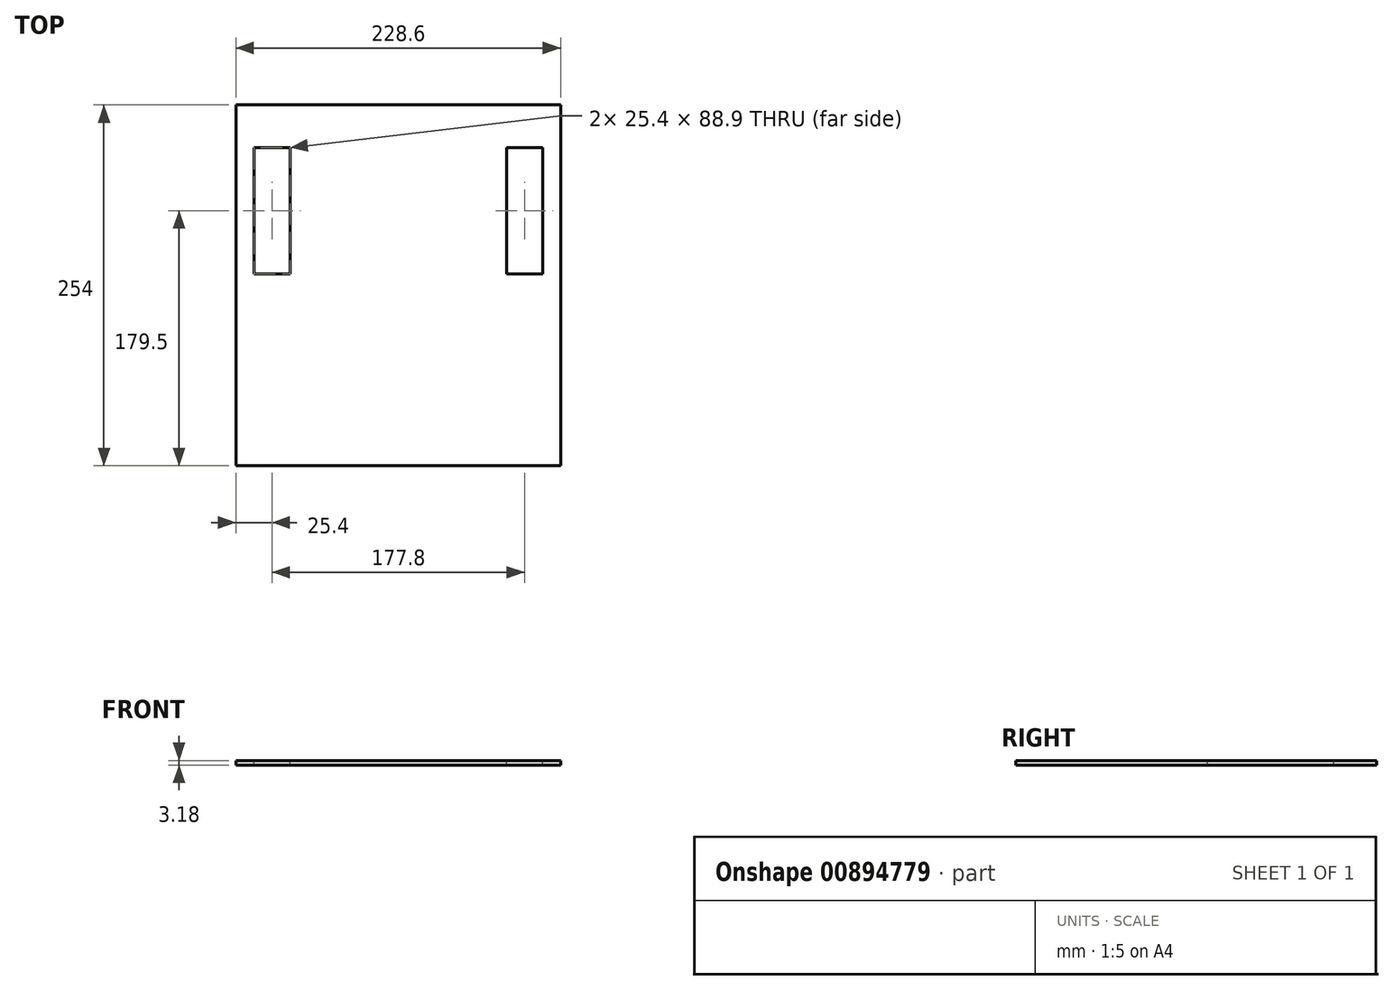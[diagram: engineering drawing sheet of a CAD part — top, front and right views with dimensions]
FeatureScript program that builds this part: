
annotation { "Feature Type Name" : "Feature", "Feature Type Description" : "" }
export const myFeature = defineFeature(function(context is Context, id is Id, definition is map)
    precondition{}
    {
        {
            var Q0;
            Q0=qCreatedBy(makeId("Top.planeOp"),FACE);
            var sketch = newSketch(context, id + "F0", { "sketchPlane" : qUnion([Q0])});
            skLineSegment(sketch, "E0.bottom", {"start": v(114.3, -127) * mm, "end": v(-114.3, -127) * mm});
            skLineSegment(sketch, "E0.top", {"start": v(114.3, 127) * mm, "end": v(-114.3, 127) * mm});
            skLineSegment(sketch, "E0.left", {"start": v(114.3, -127) * mm, "end": v(114.3, 127) * mm});
            skLineSegment(sketch, "E0.right", {"start": v(-114.3, -127) * mm, "end": v(-114.3, 127) * mm});
            skPoint(sketch, "E0.middle", {"position": v(0, 0) * mm});
            skSolve(sketch);
        }
        {
            var Q0;
            Q0=makeQuery(id+"F0.imprint","IMPRINT",FACE,{"disambiguationData":[TD([[makeQuery(id+"F0.imprint","IMPRINT",EDGE,{"derivedFrom":sQuery(id+"F0.wireOp",EDGE,"E0.bottom")}),-1.0]])]});
            extrude(context, id + "F1", {"entities" : qUnion([Q0]), "depth" : 3.17 * mm, "offsetDistance" : 25.4 * mm});
        }
        {
            var Q0;
            Q0=makeQuery(id+"F1.opExtrude","CAP_FACE",FACE,{"disambiguationData":[OSD([sQuery(id+"F0.wireOp",EDGE,"E0.bottom"),sQuery(id+"F0.wireOp",EDGE,"E0.top"),sQuery(id+"F0.wireOp",EDGE,"E0.left"),sQuery(id+"F0.wireOp",EDGE,"E0.right")])],"isStart":false});
            var sketch = newSketch(context, id + "F2", { "sketchPlane" : qUnion([Q0])});
            skLineSegment(sketch, "E1.bottom", {"start": v(-101.6, 96.95) * mm, "end": v(-76.2, 96.95) * mm});
            skLineSegment(sketch, "E1.top", {"start": v(-101.6, 8.05) * mm, "end": v(-76.2, 8.05) * mm});
            skLineSegment(sketch, "E1.left", {"start": v(-101.6, 96.95) * mm, "end": v(-101.6, 8.05) * mm});
            skLineSegment(sketch, "E1.right", {"start": v(-76.2, 96.95) * mm, "end": v(-76.2, 8.05) * mm});
            skLineSegment(sketch, "E2.MirrorCS", {"start": v(76.2, 96.95) * mm, "end": v(76.2, 8.05) * mm});
            skLineSegment(sketch, "E3.MirrorCS", {"start": v(101.6, 8.05) * mm, "end": v(76.2, 8.05) * mm});
            skLineSegment(sketch, "E4.MirrorCS", {"start": v(101.6, 96.95) * mm, "end": v(101.6, 8.05) * mm});
            skLineSegment(sketch, "E5.MirrorCS", {"start": v(101.6, 96.95) * mm, "end": v(76.2, 96.95) * mm});
            skSolve(sketch);
        }
        {
            var Q0;
            Q0=makeQuery(id+"F2.imprint","IMPRINT",FACE,{"disambiguationData":[TD([[makeQuery(id+"F2.imprint","IMPRINT",EDGE,{"derivedFrom":sQuery(id+"F2.wireOp",EDGE,"E1.bottom")}),-1.0]])]});
            var Q1;
            Q1=makeQuery(id+"F2.imprint","IMPRINT",FACE,{"disambiguationData":[TD([[makeQuery(id+"F2.imprint","IMPRINT",EDGE,{"derivedFrom":sQuery(id+"F2.wireOp",EDGE,"E2.MirrorCS")}),1.0]])]});
            extrude(context, id + "F3", {"entities" : qUnion([Q0, Q1]), "operationType" : NewBodyOperationType.REMOVE, "oppositeDirection" : true, "depth" : 25.4 * mm, "offsetDistance" : 25.4 * mm});
        }
    });
